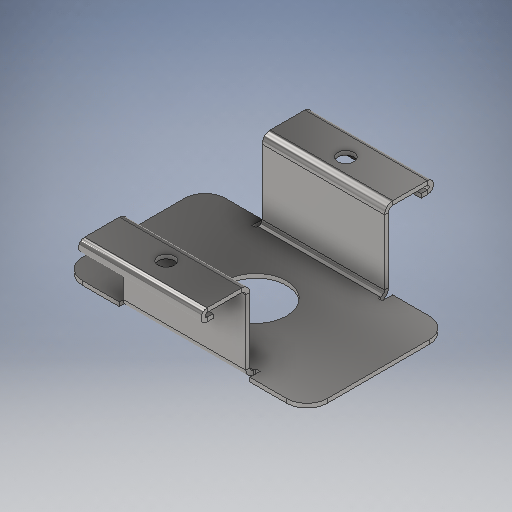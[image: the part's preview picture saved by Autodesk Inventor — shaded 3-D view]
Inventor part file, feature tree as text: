
AUTODESK INVENTOR PART (.ipt)
format: ipt  version: 2025.2 (Build 292293000, 293)  size: 429,568 bytes
history: native  units: mm
features: sheet_metal_op x15, sketch x9, other x5, hole x2, imported_body x1, chamfer x1
ambient origin geometry x8: Origin, YZ Plane, XZ Plane, XY Plane, X Axis, Y Axis, Z Axis, Center Point
bodies: Body1 (feature_tree)
feature tree (33):
  imported_body  "base"
  sheet_metal_op  "Face1"
  chamfer  "Corner Round1"
  sheet_metal_op  "Flange1"
  sheet_metal_op  "Flange2"
  sheet_metal_op  "Flange3"
  sheet_metal_op  "Flange4"
  sheet_metal_op  "Hem1"
  sheet_metal_op  "Hem2"
  hole  "Hole1"  [1 undecoded]
  hole  "Hole2"  [1 undecoded]
  sketch  "Sketch1"  dims[d0=60.0mm d1=35.0mm]
  other  "Plate1"
  sketch  "Sketch2"  dims[d2=1.0mm d3=5.0mm]
  other  "Plate2"
  sheet_metal_op  "Bend1"
  sheet_metal_op  "Corner1"
  sketch  "Sketch3"  dims[d4=1.0mm]
  other  "Plate3"
  sheet_metal_op  "Bend2"
  sheet_metal_op  "Corner2"
  sketch  "Sketch4"  dims[d5=0.5mm]
  other  "Plate4"
  sheet_metal_op  "Bend3"
  sheet_metal_op  "Corner3"
  sketch  "Sketch5"  dims[d6=2.0mm]
  other  "Plate5"
  sheet_metal_op  "Bend4"
  sheet_metal_op  "Corner4"
  sketch  "Sketch8"  dims[d11=30.0mm]
  sketch  "Sketch9"  dims[d12=4.0mm d13=1.0mm d14=1.0mm d15=1.0mm d16=0.5mm d17=2.0mm d18=1.0mm d19=20.0mm d20=90.0deg d21=1.0mm d22=30.0mm d23=4.0mm d24=1.0mm d25=1.0mm d26=1.0mm d27=0.5mm d28=2.0mm d29=1.0mm d30=12.0mm d31=90.0deg d32=1.0mm d33=4.0mm d34=1.0mm d35=1.0mm d36=1.0mm d37=0.5mm d38=2.0mm d39=1.0mm d40=12.0mm d41=90.0deg d42=1.0mm d43=4.0mm d44=1.0mm d45=1.0mm d46=1.0mm d47=0.5mm d48=2.0mm d49=1.0mm d50=3.0mm d51=1.0mm d52=0.5mm d53=1.0mm d54=0.5mm d55=2.0mm d56=1.0mm d57=3.0mm d58=1.0mm d59=0.5mm d60=5.0mm d61=4.0mm d62=6.0mm d63=4.0mm d64=2.0mm d65=90.0deg d66=1.0mm d67=20.594885mm d68=5.0mm d69=15.0mm d70=15.0mm d71=30.0mm d72=16.5mm d73=15.0mm d74=6.0mm d75=4.0mm d76=2.0mm d77=90.0deg d78=8.0mm d79=20.594885mm]
  sketch  "Sketch6"  dims[d7=1.0mm]
  sketch  "Sketch7"  dims[d8=20.0mm d9=90.0deg d10=1.0mm]
note: 2 required parameter values undecoded (feature->parameter linkage not recoverable at this tier; creation-order binding heuristic only, values carry confidence <= 0.55)
